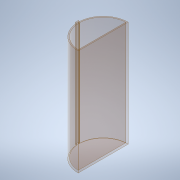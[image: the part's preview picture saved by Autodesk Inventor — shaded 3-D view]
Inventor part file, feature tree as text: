
AUTODESK INVENTOR PART (.ipt)
format: ipt  version: 2020 (Build 240168000, 168)  size: 123,392 bytes
history: native  units: mm
features: extrude x2, sketch x1
ambient origin geometry x8: Origin, YZ Plane, XZ Plane, XY Plane, X Axis, Y Axis, Z Axis, Center Point
bodies: Solid1 (feature_tree)
feature tree (3):
  sketch  "Sketch1"  dims[d0=83.0mm d1=83.0mm d2=5.0mm d4=2.2mm d5=41.5mm d6=2.0mm d7=2.0mm d8=0.0mm d9=173.0mm d10=0.0mm]
  extrude  "Extrusion1"  Depth=173.0mm
  extrude  "Extrusion2"  Depth=5.0mm
